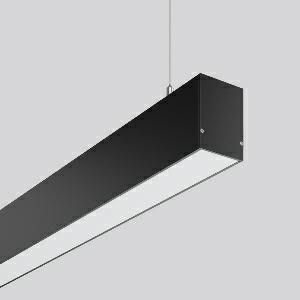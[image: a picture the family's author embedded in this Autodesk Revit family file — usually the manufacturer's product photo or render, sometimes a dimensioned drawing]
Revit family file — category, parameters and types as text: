
# Revit family: less_is_more_50_312319_003_1_76_f88b
name_source: partatom
category: Lighting Fixtures
units: mm (PartAtom-declared; Revit-internal decimal feet)

## family parameters
Cut with Voids When Loaded = No
Host = Face
Light Source = No
Part Type = Normal
Room Calculation Point = No
Round Connector Dimension = Use Diameter
Shared = No

## types (1)
- LESS IS MORE 50 (1 x LED Modul 840, 6450 lm, 4000)
    Apparent Load = 52 VA
    CIE Flux Codes = 49 80 96 63 100
    Color Rendering = 80
    Color Temperature = 4000
    Default Elevation = 1800 mm
    Description = Series: LESS IS MORE 50
Linear pendant luminaire for aesthetically sophisticated lighting. Housing: extruded aluminium profile, powder-coated. End cap aluminium powder-coated. Canopy made of aluminium, powder-coated. Diffuser made of non-yellowing plastic (PMMA), opal. Direct 65%, indirect 35% light emission. Suitable for pendant. 2-point steel cable suspension freely positionable and infinitely height-adjustable. Special lengths available on request. LED unit with integrated converter interchangeable and removable. Suitable for through-wiring. With sensors or as a safety luminaire on request. 
Colour: deep black, matt (RAL 9005)
Length: 1407 mm
Width: 57 mm
Height: 75 mm
Suspension length: 2000 mm
Lamp: LED
Socket: without socket
Colour temperature: 4000K
Colour rendering index (CRI): 80
Light source: LED
Socket lamp2: Without base
Colour temperature: 4000K
System power: 52 W
Rated luminous flux: 6450 lm
Luminous efficiency: 124 lm/W
Control gear: Converter, dimmable, DALI
Control gear: Converter, dimmable, DALI
Protection class: I
Type of protection: IP 20
    Height = 75 mm
    Lamp = 1 x LED Modul 840
    Lamp Light Flux = 6450 lm
    Lamp count = 1
    Length = 1407 mm
    Lifetime = 50000 h
    Luminous efficacy = 124 lm/W
    Manufacturer = RZB
    ModVariant = No
    Model = 312319.003.1.76
    Mounting Place = Ceiling
    Mounting Type = Pendant
    Number of Poles = 1
    OnlyDefault = Yes
    Power Factor = 1
    Product Name = LESS IS MORE 50
    Product group = Pendant LED linear luminaires
    ProductGroupID = 907
    Protection Class = Protection class I
    Protection Degree = IP 20
    RLX_Detail_Level = 1
    RLX_Emergency_Light_Flux = 0 lm
    RLX_Emergency_Type = 0
    RLX_Emergency_Type_DB = No
    RlxData = <blob elided: 39857 chars, md5=0f0ec18c>
    Socket = socket
    Standby Power = 0 W
    System Light Flux = 6450 lm
    System Power = 52 W
    Type Comments = Product without accessories
    Type Image = 312318.003.jpg
    URL = http://relux.com
    VarID = ---
    Voltage = 230 V
    Voltage Range = 220-240 V
    Weight = 0.00 kg
    Width = 57 mm

## geometry (parser evidence)
native form markers: Blend x4, Sweep x11
no freeform markers — native parametric forms only
